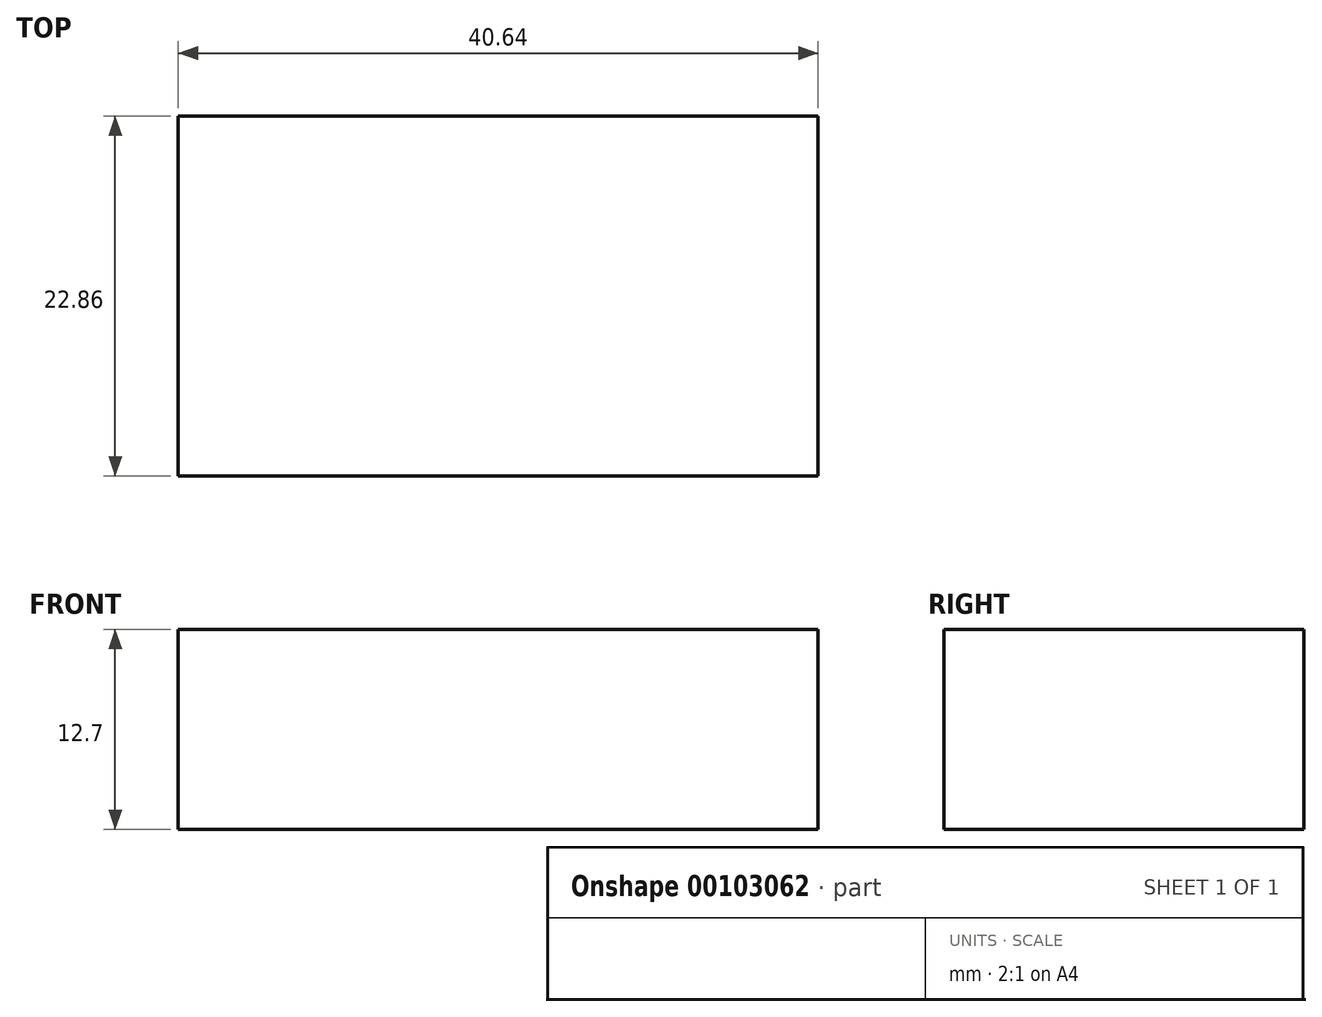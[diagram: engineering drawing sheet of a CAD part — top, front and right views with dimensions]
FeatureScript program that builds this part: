
annotation { "Feature Type Name" : "Feature", "Feature Type Description" : "" }
export const myFeature = defineFeature(function(context is Context, id is Id, definition is map)
    precondition{}
    {
        {
            var Q0;
            Q0=qCreatedBy(makeId("Top.planeOp"),FACE);
            var sketch = newSketch(context, id + "F0", { "sketchPlane" : qUnion([Q0])});
            skLineSegment(sketch, "E0.bottom", {"start": v(-18, 11) * mm, "end": v(22.63, 11) * mm});
            skLineSegment(sketch, "E0.top", {"start": v(-18, -11.86) * mm, "end": v(22.63, -11.86) * mm});
            skLineSegment(sketch, "E0.left", {"start": v(-18, 11) * mm, "end": v(-18, -11.86) * mm});
            skLineSegment(sketch, "E0.right", {"start": v(22.63, 11) * mm, "end": v(22.63, -11.86) * mm});
            skSolve(sketch);
        }
        {
            var Q0;
            Q0=makeQuery(id+"F0.imprint","IMPRINT",FACE,{"disambiguationData":[TD([[makeQuery(id+"F0.imprint","IMPRINT",EDGE,{"derivedFrom":sQuery(id+"F0.wireOp",EDGE,"E0.bottom")}),-1.0]])]});
            extrude(context, id + "F1", {"entities" : qUnion([Q0]), "depth" : 12.7 * mm});
        }
    });
